# Revit family: Hager-MINIGAMMA-Surface_mounted-IP30-Without_Cover-With_DIN-Hosted-DE-de
name_source: partatom
category: Electrical Equipment
units: mm (PartAtom-declared; Revit-internal decimal feet)

## family parameters
Cut with Voids When Loaded = No
Host = Face
Maintain Annotation Orientation = Yes
Panel Configuration = Two Columns, Circuits Across
Part Type = Panelboard
Room Calculation Point = No
Round Connector Dimension = Use Diameter
Shared = No

## types (8) — shared parameters
BC_MODEL_ID = 1554391
BC_OBJECT_ID = 513897
BC_OBJECT_VERSION = #3
Code hager = ADD-EC000214_EU
EF000003 - Montageart = Aufputz
EF000024 - UV-beständig = No
EF000049 - Tiefe = 82 mm  [stored 0.269029 ft]
EF000116 - RAL-Nummer = 9010
EF000118 - Mit Montageplatte = No
EF000266 - Anzahl der Reihen = 1
EF001062 - EMV-Ausführung = No
EF001088 - Anbaumöglichkeit = No
EF001134 - DIN-Schiene = Yes
EF005474 - Schutzart (IP) = IP30
EF006244 - Transparenter Deckel/Tür = No
EF006306 - Mit Schloss = No
EF015941 - Signaldurchlassende Tür = No
ETIM class code = EC000214
ETIM class name = Small distribution board
HG000001-Anzahl der Spalten = 1
HG000002-Mit tür = No
HG000003-Bereich = MINIGAMMA
HG000005-Dicke = 2 mm  [stored 0.00656168 ft]
HG000006-Flush mounted = No
HG000009-Doppelflügeligen Tür = No
HG000010-Asymmetrische Türen = No
HG000011-Leere Reihen von unten = No
HG000012-Türschwenkwinkel = 90.00°
HG000013-Tür links = No
HG000014-Tür rechts = Yes
HG000015-Sichtbarkeit der Türöffnung = Yes
HG000016-3D-Türsichtbarkeit = Yes
HG000017-Distanz zwischen den Polen = 18 mm  [stored 0.0590551 ft]
HG000060-RAL-number = 9010
HG000099-Onfly Template ID-de-DE = 507532
HGEF000266-Anzahl der Reihen = 1
Manufacturer = Hager
Name = MINIGAMMA-Surface_mounted-IP30-Without_Cover-With_DIN-DE
Name BIM&CO = Electricity
Name hager = ADD_Enclosures_EC000214
Uniformat = Low Tension Service & Dist.
Uniformat code = D501001
zero-valued in all types: Default Elevation, EF000218 - Einbautiefe, EF000332 - Einbauhöhe, EF000846 - Einbaubreite, EF001131 - Innentiefe, HG000007-Anzahl der leeren Spalten, HG000008-Anzahl der leeren Reihen

## per-type parameters (varying)
| type | BC_VARIANT_ID | EF000007 - Farbe | EF000008 - Breite | EF000040 - Höhe | EF002950 - Breite in Teilungseinheiten | EF004462 - Art der Schließung | EF009212 - Ausführung Deckel | EF015776 - Erdungsklemmenblock | EF015777 - Neutralleiterklemmenblock | HG000004-Herstellerreferenz | HGEF0002950-Breite in Teilungseinheiten |
| MINIGAMMA-Surface_mounted_W55_H160_D82_2_Modular_Spacing-GD102E | 1179034 | weiß | 55 mm  [stored 0.180446 ft] | 160 mm  [stored 0.524934 ft] | 2 | sonstige | mit Ausschnitt | No | No | GD102E | 2 |
| MINIGAMMA-Surface_mounted_W55_H160_D82_2_Modular_Spacing-GD102N | 1179035 |  | 55 mm  [stored 0.180446 ft] | 160 mm  [stored 0.524934 ft] | 2 |  |  | No | No | GD102N | 2 |
| MINIGAMMA-Surface_mounted_W110_H180_D82_4_Modular_Spacing-GD104N | 1179036 |  | 110 mm  [stored 0.360892 ft] | 180 mm  [stored 0.590551 ft] | 4 |  |  | Yes | Yes | GD104N | 4 |
| MINIGAMMA-Surface_mounted_W146_H180_D82_6_Modular_Spacing-GD106N | 1179037 |  | 146 mm  [stored 0.479003 ft] | 180 mm  [stored 0.590551 ft] | 6 |  |  | No | No | GD106N | 6 |
| MINIGAMMA-Surface_mounted_W182_H180_D82_8_Modular_Spacing-GD108E | 1179038 |  | 182 mm  [stored 0.597113 ft] | 180 mm  [stored 0.590551 ft] | 8 |  |  | No | No | GD108E | 8 |
| MINIGAMMA-Surface_mounted_W182_H180_D82_8_Modular_Spacing-GD108N | 1179039 |  | 182 mm  [stored 0.597113 ft] | 180 mm  [stored 0.590551 ft] | 8 |  |  | No | No | GD108N | 8 |
| MINIGAMMA-Surface_mounted_W218_H180_D82_10_Modular_Spacing-GD110E | 1179040 |  | 218 mm  [stored 0.715223 ft] | 180 mm  [stored 0.590551 ft] | 10 |  |  | No | No | GD110E | 10 |
| MINIGAMMA-Surface_mounted_W218_H180_D82_10_Modular_Spacing-GD110N | 1179041 |  | 218 mm  [stored 0.715223 ft] | 180 mm  [stored 0.590551 ft] | 10 |  |  | No | No | GD110N | 10 |

note: column(s) folded — value = type name in every type: Reference

note: [stored X ft] marks values corroborated as IEEE doubles in the binary element streams (Revit-internal decimal feet)

## geometry (parser evidence)
native form markers: Sweep x14
no freeform markers — native parametric forms only
